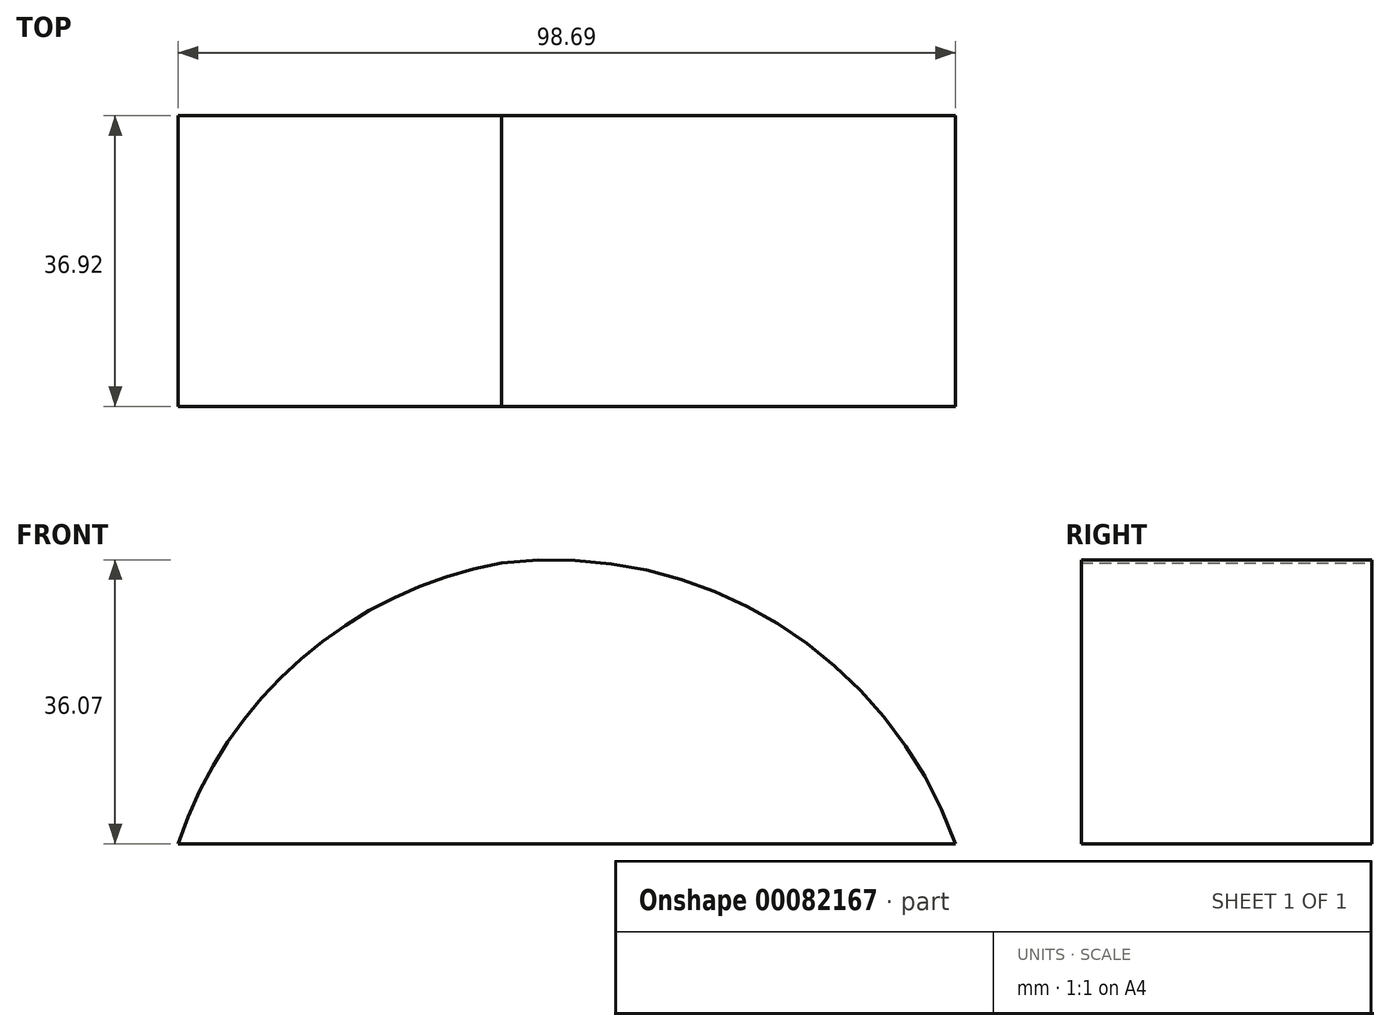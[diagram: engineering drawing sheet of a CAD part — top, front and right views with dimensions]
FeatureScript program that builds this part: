
annotation { "Feature Type Name" : "Feature", "Feature Type Description" : "" }
export const myFeature = defineFeature(function(context is Context, id is Id, definition is map)
    precondition{}
    {
        {
            var Q0;
            Q0=qCreatedBy(makeId("Front.planeOp"),FACE);
            var sketch = newSketch(context, id + "F0", { "sketchPlane" : qUnion([Q0])});
            skArc(sketch, "E0", {"start": v(0, 35.67) * mm, "mid": v(-25.45, 23.5) * mm, "end": v(-41.04, 0) * mm});
            skArc(sketch, "E1", {"start": v(57.65, 0) * mm, "mid": v(35.1, 27.96) * mm, "end": v(0, 35.67) * mm});
            skLineSegment(sketch, "E2", {"start": v(-41.04, 0) * mm, "end": v(57.65, 0) * mm});
            skSolve(sketch);
        }
        {
            var Q0;
            Q0=makeQuery(id+"F0.imprint","IMPRINT",FACE,{"disambiguationData":[TD([[makeQuery(id+"F0.imprint","IMPRINT",EDGE,{"derivedFrom":sQuery(id+"F0.wireOp",EDGE,"E0")}),1.0]])]});
            extrude(context, id + "F1", {"entities" : qUnion([Q0]), "depth" : 36.92 * mm});
        }
    });
